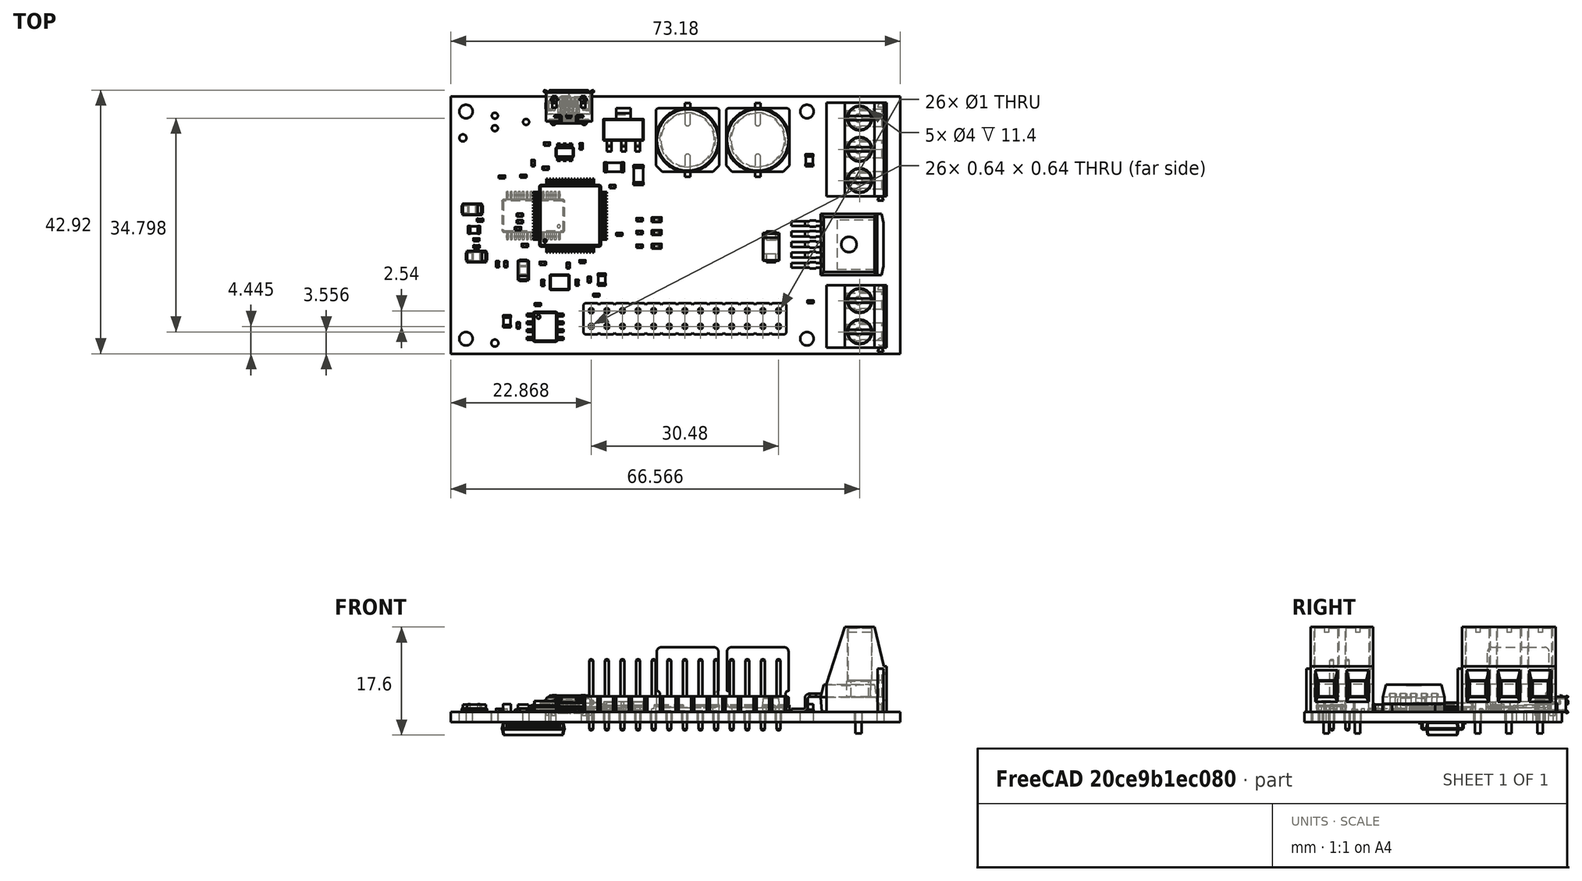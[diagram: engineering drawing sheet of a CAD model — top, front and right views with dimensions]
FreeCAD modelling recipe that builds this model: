
FCSTD DOCUMENT  (FreeCAD 0.20R29410 (Git))
Label: case
License: All rights reserved
LicenseURL: http://en.wikipedia.org/wiki/All_rights_reserved
objects: Part::Feature×1, PartDesign::FeatureBase×1, Sketcher::SketchObject×1, PartDesign::Body×1
note: 4 computed .brp shape members not serialized (recipe doc carries the construction recipe); baked Part::Feature solids carry a one-line shape summary decoded from their .brp

FEATURE [Part::Feature] Feature  label="electric_angle_actuator"
  shape: bbox 73.19 x 42.92 x 17.6 mm, 4606 faces, 57 solids (baked)
FEATURE [PartDesign::FeatureBase] BaseFeature
  BaseFeature = -> Feature
FEATURE [Sketcher::SketchObject] Sketch
  ExternalGeometry = -> [BaseFeature]
  FullyConstrained = false
  MapMode = 5
  Support = -> [XY_Plane]
  sketch-geometry (8):
    g0: LineSegment StartX=122.681 StartY=-104.294 StartZ=0 EndX=203.976 EndY=-104.294 EndZ=0
    g1: LineSegment StartX=203.976 StartY=-104.294 StartZ=0 EndX=203.976 EndY=-55.3303 EndZ=0
    g2: LineSegment StartX=203.976 StartY=-55.3303 StartZ=0 EndX=122.681 EndY=-55.3303 EndZ=0
    g3: LineSegment StartX=122.681 StartY=-55.3303 StartZ=0 EndX=122.681 EndY=-104.294 EndZ=0
    g4: LineSegment StartX=124.89 StartY=-101.852 StartZ=0 EndX=201.767 EndY=-101.852 EndZ=0
    g5: LineSegment StartX=201.767 StartY=-101.852 StartZ=0 EndX=201.767 EndY=-57.0749 EndZ=0
    g6: LineSegment StartX=201.767 StartY=-57.0749 StartZ=0 EndX=124.89 EndY=-57.0749 EndZ=0
    g7: LineSegment StartX=124.89 StartY=-57.0749 StartZ=0 EndX=124.89 EndY=-101.852 EndZ=0
  constraints (16):
    c: Coincident(g0,g1)
    c: Coincident(g1,g2)
    c: Coincident(g2,g3)
    c: Coincident(g3,g0)
    c: Horizontal(g0)
    c: Horizontal(g2)
    c: Vertical(g1)
    c: Vertical(g3)
    c: Coincident(g4,g5)
    c: Coincident(g5,g6)
    c: Coincident(g6,g7)
    c: Coincident(g7,g4)
    c: Horizontal(g4)
    c: Horizontal(g6)
    c: Vertical(g5)
    c: Vertical(g7)
FEATURE [PartDesign::Body] Body
  BaseFeature = -> Feature
  Group = -> [BaseFeature,Sketch]
  Origin = -> Origin
  Tip = -> BaseFeature
